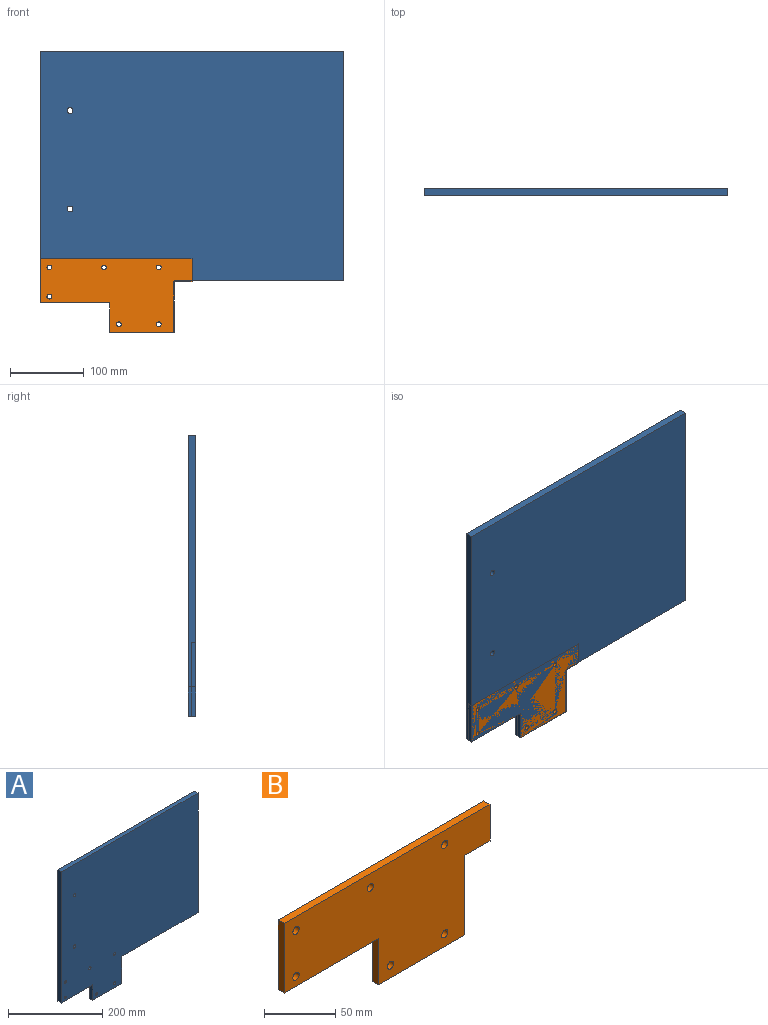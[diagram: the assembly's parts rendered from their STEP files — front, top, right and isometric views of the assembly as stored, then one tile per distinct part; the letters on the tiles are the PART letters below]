
ASSEMBLY  parts=2 mates=1
PART A: 18 faces, bbox 410x10x380 mm
  f0: plane 410x10mm, normal (0,0,1), area 4100mm2, adj f1,f7,f8,f9
  f1: plane 340x10mm, normal (-1,0,0), area 3400mm2, adj f0,f2,f8,f9
  f2: plane 94x10mm, normal (0,0,-1), area 940mm2, adj f1,f3,f8,f9
  f3: plane 40x10mm, normal (-1,0,0), area 400mm2, adj f2,f4,f8,f9
  f4: plane 87x10mm, normal (0,0,-1), area 870mm2, adj f3,f5,f8,f9
  f5: plane 70x10mm, normal (1,0,0), area 700mm2, adj f4,f6,f8,f9
  f6: plane 229x10mm, normal (0,0,-1), area 2290mm2, adj f5,f7,f8,f9
  f7: plane 310x10mm, normal (1,0,0), area 3100mm2, adj f0,f6,f8,f9
  f8: plane 410x380mm, normal (0,1,0), area 135710.4mm2, adj f0,f1,f2,f3,f4,f5,f6,f7
  f9: plane 410x380mm, normal (0,-1,0), area 135710.4mm2, adj f0,f1,f2,f3,f4,f5,f6,f7
  f10: cylinder r=3.25mm len=10mm, axis (0,-1,0), area 204.2mm2, adj f8,f9
  f11: cylinder r=3.25mm len=10mm, axis (0,-1,0), area 204.2mm2, adj f8,f9
  f12: cylinder r=3.25mm len=10mm, axis (0,-1,0), area 204.2mm2, adj f8,f9
  f13: cylinder r=3.25mm len=10mm, axis (0,-1,0), area 204.2mm2, adj f8,f9
  f14: cylinder r=3.25mm len=10mm, axis (0,-1,0), area 204.2mm2, adj f8,f9
  f15: cylinder r=3.25mm len=10mm, axis (0,-1,0), area 204.2mm2, adj f8,f9
  f16: cylinder r=4mm len=10mm, axis (0,-1,0), area 251.3mm2, adj f8,f9
  f17: cylinder r=4mm len=10mm, axis (0,-1,0), area 251.3mm2, adj f8,f9
PART B: 16 faces, bbox 205x6x100 mm
  f0: plane 205x6mm, normal (0,0,1), area 1230mm2, adj f1,f7,f8,f9
  f1: plane 60x6mm, normal (-1,0,0), area 360mm2, adj f0,f2,f8,f9
  f2: plane 94x6mm, normal (0,0,-1), area 564mm2, adj f1,f3,f8,f9
  f3: plane 40x6mm, normal (-1,0,0), area 240mm2, adj f2,f4,f8,f9
  f4: plane 86x6mm, normal (0,0,-1), area 516mm2, adj f3,f5,f8,f9
  f5: plane 68.5x6mm, normal (1,0,0), area 411mm2, adj f4,f6,f8,f9
  f6: plane 25x6mm, normal (0,0,-1), area 150mm2, adj f5,f7,f8,f9
  f7: plane 31.5x6mm, normal (1,0,0), area 189mm2, adj f0,f6,f8,f9
  f8: plane 205x100mm, normal (0,-1,0), area 14840.5mm2, adj f0,f1,f2,f3,f4,f5,f6,f7
  f9: plane 205x100mm, normal (0,1,0), area 14840.5mm2, adj f0,f1,f2,f3,f4,f5,f6,f7
  f10: cylinder r=3.15mm len=6.3mm, axis (0,-1,0), area 118.8mm2, adj f8,f9
  f11: cylinder r=3.15mm len=6.3mm, axis (0,-1,0), area 118.8mm2, adj f8,f9
  f12: cylinder r=3.15mm len=6.3mm, axis (0,-1,0), area 118.8mm2, adj f8,f9
  f13: cylinder r=3.15mm len=6.3mm, axis (0,-1,0), area 118.8mm2, adj f8,f9
  f14: cylinder r=3.15mm len=6.3mm, axis (0,-1,0), area 118.8mm2, adj f8,f9
  f15: cylinder r=3.15mm len=6.3mm, axis (0,-1,0), area 118.8mm2, adj f8,f9
PLACE A t=(35.49,-45.06,-2.74)mm
PLACE B t=(-258.92,-39.06,-56.68)mm
MATE fastened B.f10 <-> A.f14  axis (0,-1,0) through (-351.67,-45.06,-18.68)mm
